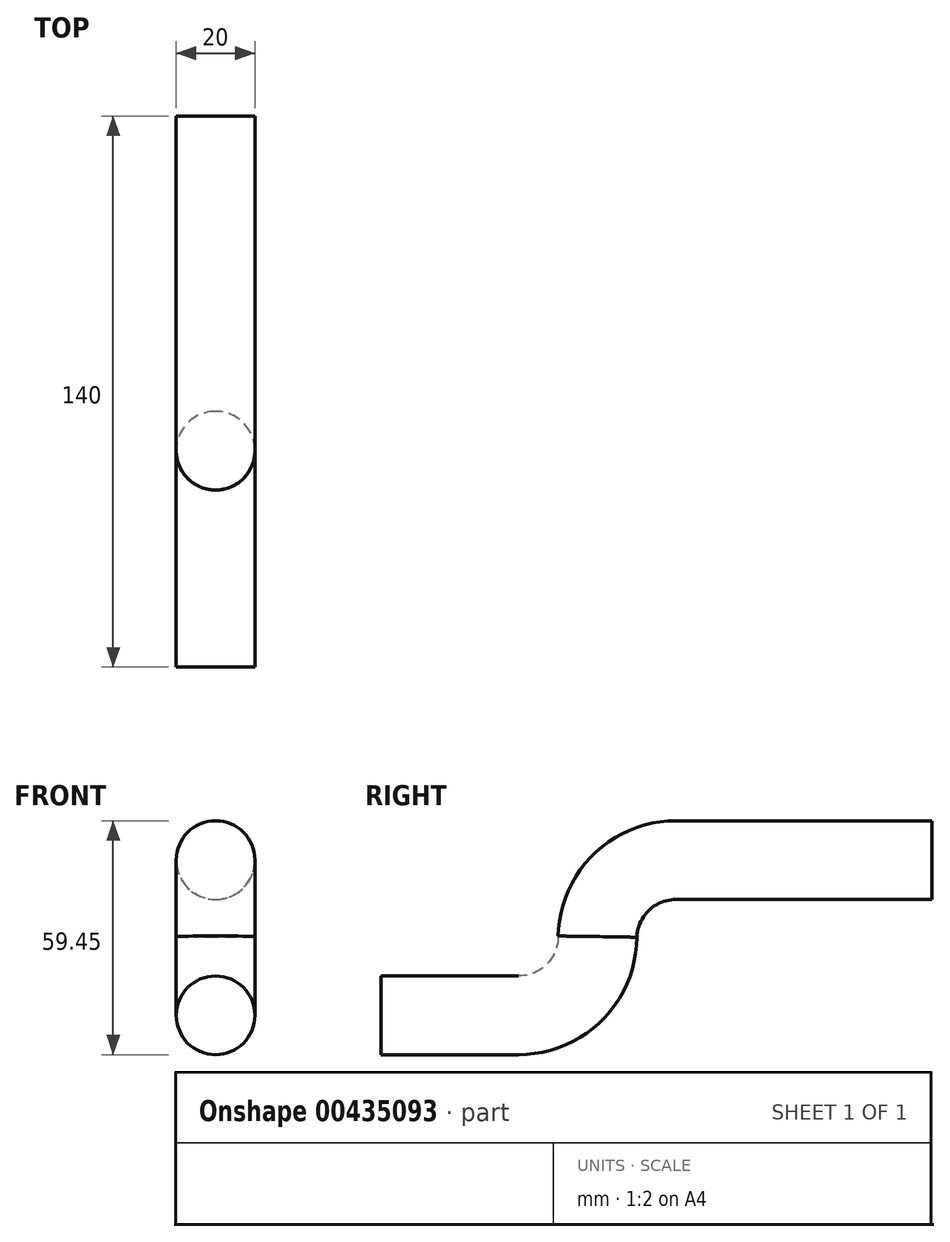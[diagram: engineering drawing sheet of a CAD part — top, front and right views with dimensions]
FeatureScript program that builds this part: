
annotation { "Feature Type Name" : "Feature", "Feature Type Description" : "" }
export const myFeature = defineFeature(function(context is Context, id is Id, definition is map)
    precondition{}
    {
        {
            var Q0;
            Q0=qCreatedBy(makeId("Front.planeOp"),FACE);
            var sketch = newSketch(context, id + "F0", { "sketchPlane" : qUnion([Q0])});
            skCircle(sketch, "E0", {"center": v(0, 0) * mm, "radius": 10 * mm});
            skSolve(sketch);
        }
        {
            var Q0;
            Q0=qCreatedBy(makeId("Right.planeOp"),FACE);
            var sketch = newSketch(context, id + "F1", { "sketchPlane" : qUnion([Q0])});
            skLineSegment(sketch, "E1", {"start": v(0, 0) * mm, "end": v(35, 0) * mm});
            skArc(sketch, "E2", {"start": v(35, 0) * mm, "mid": v(49.14, 5.86) * mm, "end": v(55, 20) * mm});
            skArc(sketch, "E3", {"start": v(75, 39.45) * mm, "mid": v(61.05, 33.79) * mm, "end": v(55, 20) * mm});
            skLineSegment(sketch, "E4", {"start": v(75, 39.45) * mm, "end": v(140, 39.45) * mm});
            skSolve(sketch);
        }
        {
            var Q0;
            Q0 = qSketchRegion(id + "F0", true);
            var Q1;
            Q1 = qConstructionFilter(qBodyType(qCreatedBy(id + "F1" ,EDGE), BodyType.WIRE), ConstructionObject.NO);
            sweep(context, id + "F2", {"profiles" : qUnion([Q0]), "path" : qUnion([Q1])});
        }
    });
